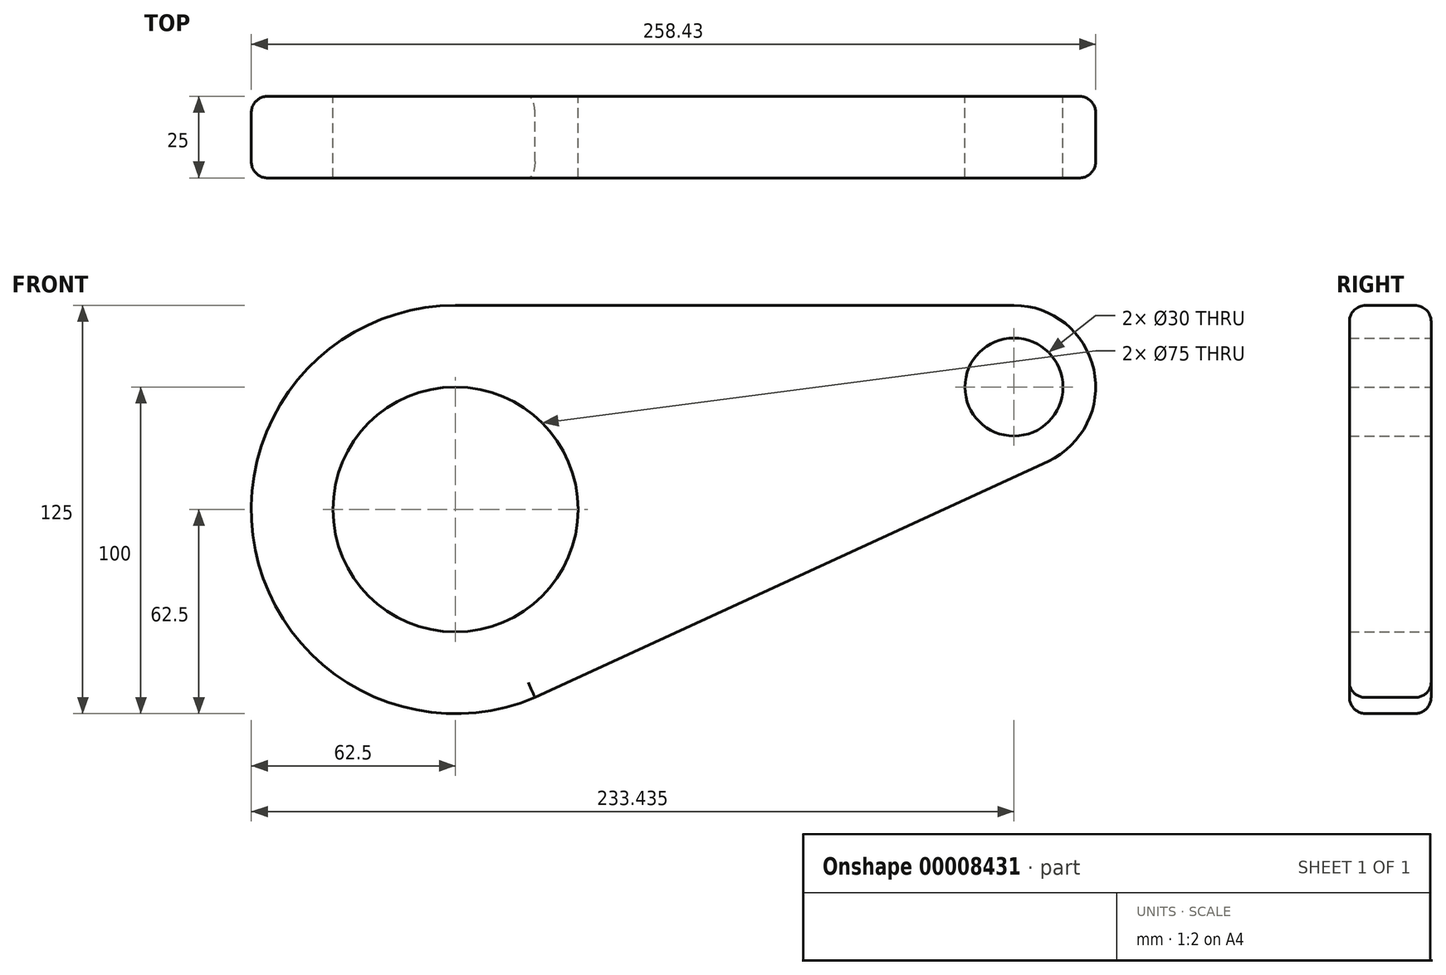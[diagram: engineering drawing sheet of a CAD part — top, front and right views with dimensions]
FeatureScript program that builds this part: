
annotation { "Feature Type Name" : "Feature", "Feature Type Description" : "" }
export const myFeature = defineFeature(function(context is Context, id is Id, definition is map)
    precondition{}
    {
        {
            var Q0;
            Q0=qCreatedBy(makeId("Front.planeOp"),FACE);
            var sketch = newSketch(context, id + "F0", { "sketchPlane" : qUnion([Q0])});
            skCircle(sketch, "E0", {"center": v(0, 0) * mm, "radius": 62.5 * mm});
            skCircle(sketch, "E1", {"center": v(170.93, 37.5) * mm, "radius": 25 * mm});
            skLineSegment(sketch, "E2", {"start": v(0, 0) * mm, "end": v(170.93, 37.5) * mm});
            skLineSegment(sketch, "E3", {"start": v(0, 62.5) * mm, "end": v(170.93, 62.5) * mm});
            skLineSegment(sketch, "E4", {"start": v(24.32, -57.57) * mm, "end": v(181.4, 14.8) * mm});
            skCircle(sketch, "E5", {"center": v(0, 0) * mm, "radius": 37.5 * mm});
            skCircle(sketch, "E6", {"center": v(170.93, 37.5) * mm, "radius": 15 * mm});
            skSolve(sketch);
        }
        {
            var Q0;
            {var subQ0=sQuery(id+"F0.wireOp",EDGE,"E3");Q0=makeQuery(id+"F0.imprint","IMPRINT",FACE,{"disambiguationData":[TD([[makeQuery(id+"F0.imprint","IMPRINT",EDGE,{"derivedFrom":subQ0}),-1.0]])]});}
            var Q1;
            {var subQ1=sQuery(id+"F0.wireOp",EDGE,"E0");var subQ5=sQuery(id+"F0.wireOp",EDGE,"E2");var subQ7=makeQuery(id+"F0.imprint","INTERSECT",VERTEX,{"derivedFrom":[subQ1,subQ5]});Q1=makeQuery(id+"F0.imprint","IMPRINT",FACE,{"disambiguationData":[TD([[makeQuery(id+"F0.imprint","IMPRINT",EDGE,{"disambiguationData":[TD([[subQ7,1.0]])],"derivedFrom":subQ1}),-1.0]])]});}
            var Q2;
            Q2=makeQuery(id+"F0.imprint","IMPRINT",FACE,{"disambiguationData":[TD([[makeQuery(id+"F0.imprint","IMPRINT",EDGE,{"derivedFrom":sQuery(id+"F0.wireOp",EDGE,"E5")}),-1.0]])]});
            var Q3;
            Q3=makeQuery(id+"F0.imprint","IMPRINT",FACE,{"disambiguationData":[TD([[makeQuery(id+"F0.imprint","IMPRINT",EDGE,{"derivedFrom":sQuery(id+"F0.wireOp",EDGE,"E6")}),-1.0]])]});
            extrude(context, id + "F1", {"entities" : qUnion([Q0, Q1, Q2, Q3]), "depth" : 25 * mm});
        }
        {
            var Q0;
            Q0=makeQuery(id+"F1.opExtrude","CAP_EDGE",EDGE,{"disambiguationData":[OSD([sQuery(id+"F0.wireOp",EDGE,"E3")])],"isStart":true});
            var Q1;
            Q1=makeQuery(id+"F1.opExtrude","CAP_EDGE",EDGE,{"disambiguationData":[OSD([sQuery(id+"F0.wireOp",EDGE,"E3")])],"isStart":false});
            fillet(context, id + "F2", {"entities" : qUnion([Q0, Q1]), "radius" : 5 * mm, "tangentPropagation" : true, "allowEdgeOverflow" : false});
        }
    });
